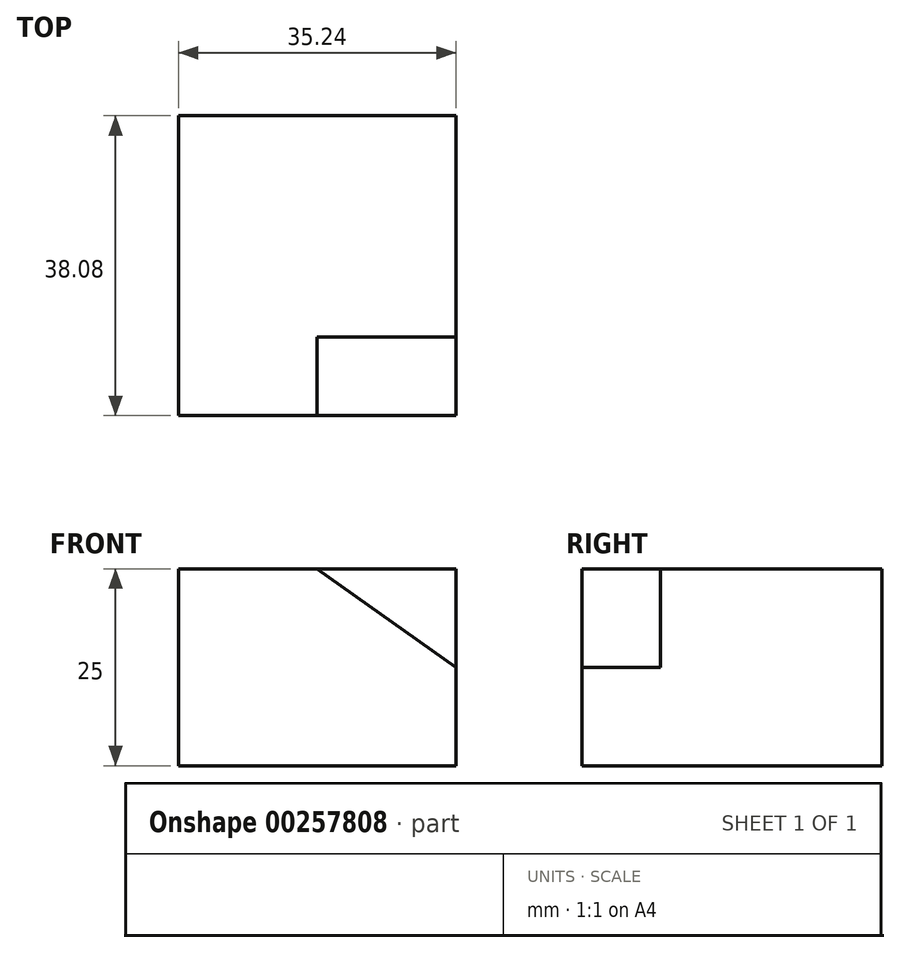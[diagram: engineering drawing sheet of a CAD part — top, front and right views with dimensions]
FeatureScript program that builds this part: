
annotation { "Feature Type Name" : "Feature", "Feature Type Description" : "" }
export const myFeature = defineFeature(function(context is Context, id is Id, definition is map)
    precondition{}
    {
        {
            var Q0;
            Q0=qCreatedBy(makeId("Top.planeOp"),FACE);
            var sketch = newSketch(context, id + "F0", { "sketchPlane" : qUnion([Q0])});
            skLineSegment(sketch, "E0.bottom", {"start": v(-132.76, -62.54) * mm, "end": v(-97.52, -62.54) * mm});
            skLineSegment(sketch, "E0.top", {"start": v(-132.76, -24.46) * mm, "end": v(-97.52, -24.46) * mm});
            skLineSegment(sketch, "E0.left", {"start": v(-132.76, -62.54) * mm, "end": v(-132.76, -24.46) * mm});
            skLineSegment(sketch, "E0.right", {"start": v(-97.52, -62.54) * mm, "end": v(-97.52, -24.46) * mm});
            skSolve(sketch);
        }
        {
            var Q0;
            Q0=makeQuery(id+"F0.imprint","IMPRINT",FACE,{"disambiguationData":[TD([[makeQuery(id+"F0.imprint","IMPRINT",EDGE,{"derivedFrom":sQuery(id+"F0.wireOp",EDGE,"E0.bottom")}),1.0]])]});
            extrude(context, id + "F1", {"entities" : qUnion([Q0]), "depth" : 25 * mm});
        }
        {
            var Q0;
            Q0=makeQuery(id+"F1.opExtrude","SWEPT_FACE",FACE,{"disambiguationData":[OSD([sQuery(id+"F0.wireOp",EDGE,"E0.bottom")])]});
            var sketch = newSketch(context, id + "F2", { "sketchPlane" : qUnion([Q0])});
            skLineSegment(sketch, "E1", {"start": v(-97.52, 12.5) * mm, "end": v(-115.14, 25) * mm});
            skLineSegment(sketch, "E2", {"start": v(-115.14, 25) * mm, "end": v(-97.52, 37.98) * mm});
            skLineSegment(sketch, "E3", {"start": v(-97.52, 37.98) * mm, "end": v(-86, 37.98) * mm});
            skLineSegment(sketch, "E4", {"start": v(-86, 37.98) * mm, "end": v(-97.52, 12.5) * mm});
            skSolve(sketch);
        }
        {
            var Q0;
            {var subQ0=sQuery(id+"F2.wireOp",EDGE,"E1");Q0=makeQuery(id+"F2.imprint","IMPRINT",FACE,{"disambiguationData":[TD([[makeQuery(id+"F2.imprint","IMPRINT",EDGE,{"derivedFrom":subQ0}),-1.0]])]});}
            extrude(context, id + "F3", {"entities" : qUnion([Q0]), "operationType" : NewBodyOperationType.REMOVE, "oppositeDirection" : true, "depth" : 10 * mm});
        }
    });
